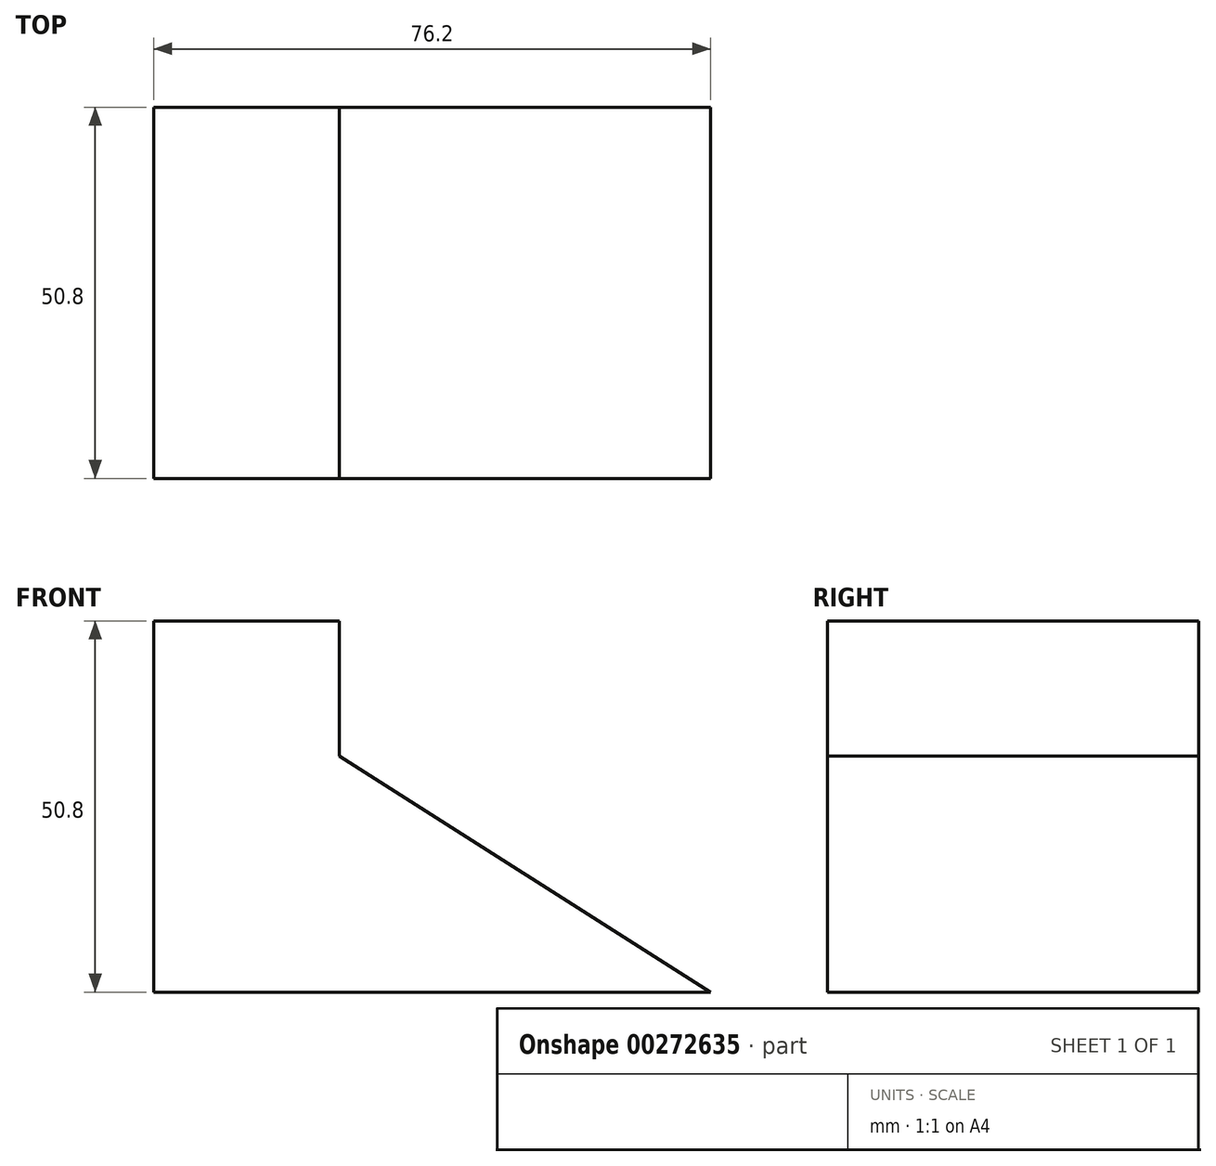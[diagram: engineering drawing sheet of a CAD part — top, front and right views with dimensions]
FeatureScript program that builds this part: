
annotation { "Feature Type Name" : "Feature", "Feature Type Description" : "" }
export const myFeature = defineFeature(function(context is Context, id is Id, definition is map)
    precondition{}
    {
        {
            var Q0;
            Q0=qCreatedBy(makeId("Front.planeOp"),FACE);
            var sketch = newSketch(context, id + "F0", { "sketchPlane" : qUnion([Q0])});
            skLineSegment(sketch, "E0", {"start": v(-32.27, 18.53) * mm, "end": v(-32.27, -32.27) * mm});
            skLineSegment(sketch, "E1", {"start": v(-32.27, -32.27) * mm, "end": v(43.93, -32.27) * mm});
            skLineSegment(sketch, "E2", {"start": v(-32.27, 18.53) * mm, "end": v(-6.87, 18.53) * mm});
            skLineSegment(sketch, "E3", {"start": v(-6.87, 18.53) * mm, "end": v(-6.87, 0) * mm});
            skLineSegment(sketch, "E4", {"start": v(-6.87, 0) * mm, "end": v(43.93, -32.27) * mm});
            skSolve(sketch);
        }
        {
            var Q0;
            Q0 = qSketchRegion(id + "F0", true);
            extrude(context, id + "F1", {"entities" : qUnion([Q0]), "depth" : 50.8 * mm});
        }
    });
